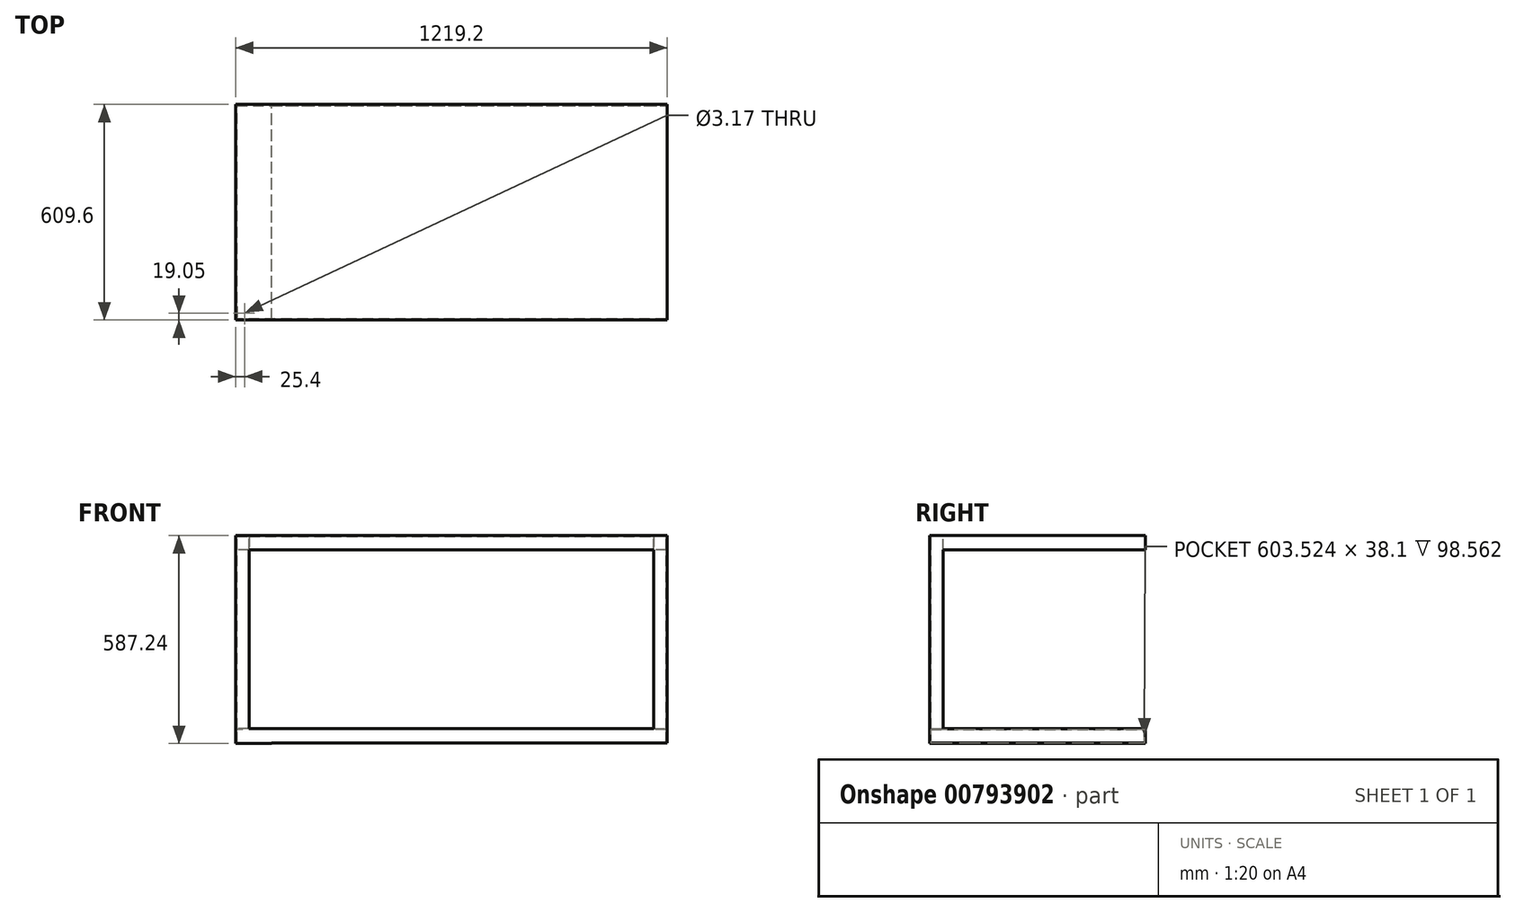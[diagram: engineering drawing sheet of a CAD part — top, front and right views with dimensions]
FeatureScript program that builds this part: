
annotation { "Feature Type Name" : "Feature", "Feature Type Description" : "" }
export const myFeature = defineFeature(function(context is Context, id is Id, definition is map)
    precondition{}
    {
        {
            var Q0;
            Q0=qCreatedBy(makeId("Top.planeOp"),FACE);
            var sketch = newSketch(context, id + "F0", { "sketchPlane" : qUnion([Q0])});
            skLineSegment(sketch, "E0.bottom", {"start": v(609.6, 304.8) * mm, "end": v(-609.6, 304.8) * mm});
            skLineSegment(sketch, "E0.top", {"start": v(609.6, -304.8) * mm, "end": v(-609.6, -304.8) * mm});
            skLineSegment(sketch, "E0.left", {"start": v(609.6, 304.8) * mm, "end": v(609.6, -304.8) * mm});
            skLineSegment(sketch, "E0.right", {"start": v(-609.6, 304.8) * mm, "end": v(-609.6, -304.8) * mm});
            skPoint(sketch, "E0.middle", {"position": v(0, 0) * mm});
            skSolve(sketch);
        }
        {
            var Q0;
            Q0=qSketchRegion(id+"F0",true);
            extrude(context, id + "F1", {"entities" : qUnion([Q0]), "oppositeDirection" : true, "depth" : 1.52 * mm, "offsetDistance" : 25.4 * mm});
        }
        {
            var Q0;
            Q0=makeQuery(id+"F1.opExtrude","CAP_FACE",FACE,{"disambiguationData":[OSD([sQuery(id+"F0.wireOp",EDGE,"E0.bottom"),sQuery(id+"F0.wireOp",EDGE,"E0.top"),sQuery(id+"F0.wireOp",EDGE,"E0.left"),sQuery(id+"F0.wireOp",EDGE,"E0.right")])],"isStart":false});
            var sketch = newSketch(context, id + "F2", { "sketchPlane" : qUnion([Q0])});
            skLineSegment(sketch, "E1", {"start": v(-609.6, 304.8) * mm, "end": v(609.6, 304.8) * mm});
            skLineSegment(sketch, "E2", {"start": v(609.6, 304.8) * mm, "end": v(609.6, -304.8) * mm});
            skLineSegment(sketch, "E3", {"start": v(609.6, -304.8) * mm, "end": v(-609.6, -304.8) * mm});
            skLineSegment(sketch, "E4", {"start": v(-609.6, -304.8) * mm, "end": v(-609.6, 304.8) * mm});
            skLineSegment(sketch, "E5.0", {"start": v(-608.08, -303.28) * mm, "end": v(-608.08, 303.28) * mm});
            skLineSegment(sketch, "E6.0", {"start": v(-608.08, 303.28) * mm, "end": v(608.08, 303.28) * mm});
            skLineSegment(sketch, "E7.0", {"start": v(608.08, 303.28) * mm, "end": v(608.08, -303.28) * mm});
            skLineSegment(sketch, "E8.0", {"start": v(608.08, -303.28) * mm, "end": v(-608.08, -303.28) * mm});
            skSolve(sketch);
        }
        {
            var Q0;
            Q0=qSketchRegion(id+"F2",true);
            extrude(context, id + "F3", {"entities" : qUnion([Q0]), "operationType" : NewBodyOperationType.ADD, "depth" : 38.1 * mm, "offsetDistance" : 25.4 * mm});
        }
        {
            var Q0;
            Q0=makeQuery(id+"F1.opExtrude","CAP_FACE",FACE,{"disambiguationData":[OSD([sQuery(id+"F0.wireOp",EDGE,"E0.bottom"),sQuery(id+"F0.wireOp",EDGE,"E0.top"),sQuery(id+"F0.wireOp",EDGE,"E0.left"),sQuery(id+"F0.wireOp",EDGE,"E0.right")])],"isStart":false});
            var sketch = newSketch(context, id + "F4", { "sketchPlane" : qUnion([Q0])});
            skLineSegment(sketch, "E9", {"start": v(-571.5, 304.8) * mm, "end": v(-609.6, 304.8) * mm});
            skLineSegment(sketch, "E10", {"start": v(-609.6, 304.8) * mm, "end": v(-609.6, 266.7) * mm});
            skLineSegment(sketch, "E11", {"start": v(-609.6, 266.7) * mm, "end": v(-606.56, 266.7) * mm});
            skLineSegment(sketch, "E12", {"start": v(-606.56, 266.7) * mm, "end": v(-606.56, 301.76) * mm});
            skLineSegment(sketch, "E13", {"start": v(-606.56, 301.76) * mm, "end": v(-571.5, 301.76) * mm});
            skLineSegment(sketch, "E14", {"start": v(-571.5, 301.76) * mm, "end": v(-571.5, 304.8) * mm});
            skLineSegment(sketch, "E15.MirrorCS", {"start": v(571.5, 301.76) * mm, "end": v(571.5, 304.8) * mm});
            skLineSegment(sketch, "E16.MirrorCS", {"start": v(609.6, 266.7) * mm, "end": v(606.56, 266.7) * mm});
            skLineSegment(sketch, "E17.MirrorCS", {"start": v(606.56, 301.76) * mm, "end": v(571.5, 301.76) * mm});
            skLineSegment(sketch, "E18.MirrorCS", {"start": v(606.56, 266.7) * mm, "end": v(606.56, 301.76) * mm});
            skLineSegment(sketch, "E19.MirrorCS", {"start": v(571.5, 304.8) * mm, "end": v(609.6, 304.8) * mm});
            skLineSegment(sketch, "E20.MirrorCS", {"start": v(609.6, 304.8) * mm, "end": v(609.6, 266.7) * mm});
            skSolve(sketch);
        }
        {
            var Q0;
            Q0=qSketchRegion(id+"F4",true);
            extrude(context, id + "F5", {"entities" : qUnion([Q0]), "operationType" : NewBodyOperationType.ADD, "depth" : 584.2 * mm, "offsetDistance" : 25.4 * mm});
        }
        {
            var Q0;
            Q0=makeQuery(id+"F1.opExtrude","CAP_FACE",FACE,{"disambiguationData":[OSD([sQuery(id+"F0.wireOp",EDGE,"E0.bottom"),sQuery(id+"F0.wireOp",EDGE,"E0.top"),sQuery(id+"F0.wireOp",EDGE,"E0.left"),sQuery(id+"F0.wireOp",EDGE,"E0.right")])],"isStart":true});
            cPlane(context, id + "F6", {"entities" : qUnion([Q0]), "cplaneType" : CPlaneType.OFFSET, "offset" : 546.1 * mm, "oppositeDirection" : true, "width" : 152.4 * mm, "height" : 152.4 * mm});
        }
        {
            var Q0;
            Q0=qCreatedBy(id+"F6.planeOp",FACE);
            var sketch = newSketch(context, id + "F7", { "sketchPlane" : qUnion([Q0])});
            skLineSegment(sketch, "E21.bottom", {"start": v(-609.6, 304.8) * mm, "end": v(609.6, 304.8) * mm});
            skLineSegment(sketch, "E21.top", {"start": v(-609.6, -304.8) * mm, "end": v(609.6, -304.8) * mm});
            skLineSegment(sketch, "E21.left", {"start": v(-609.6, 304.8) * mm, "end": v(-609.6, -304.8) * mm});
            skLineSegment(sketch, "E21.right", {"start": v(609.6, 304.8) * mm, "end": v(609.6, -304.8) * mm});
            skPoint(sketch, "E21.middle", {"position": v(0, 0) * mm});
            skSolve(sketch);
        }
        {
            var Q0;
            Q0=qSketchRegion(id+"F7",true);
            extrude(context, id + "F8", {"entities" : qUnion([Q0]), "operationType" : NewBodyOperationType.ADD, "oppositeDirection" : true, "depth" : 1.52 * mm, "offsetDistance" : 25.4 * mm});
        }
        {
            var Q0;
            Q0=makeQuery(id+"F8.opExtrude","CAP_FACE",FACE,{"disambiguationData":[OSD([sQuery(id+"F7.wireOp",EDGE,"E21.bottom"),sQuery(id+"F7.wireOp",EDGE,"E21.top"),sQuery(id+"F7.wireOp",EDGE,"E21.left"),sQuery(id+"F7.wireOp",EDGE,"E21.right")])],"isStart":false});
            var sketch = newSketch(context, id + "F9", { "sketchPlane" : qUnion([Q0])});
            skLineSegment(sketch, "E22.bottom", {"start": v(-609.6, 304.8) * mm, "end": v(609.6, 304.8) * mm});
            skLineSegment(sketch, "E22.top", {"start": v(-609.6, -304.8) * mm, "end": v(609.6, -304.8) * mm});
            skLineSegment(sketch, "E22.left", {"start": v(-609.6, 304.8) * mm, "end": v(-609.6, -304.8) * mm});
            skLineSegment(sketch, "E22.right", {"start": v(609.6, 304.8) * mm, "end": v(609.6, -304.8) * mm});
            skPoint(sketch, "E22.middle", {"position": v(0, 0) * mm});
            skLineSegment(sketch, "E23.bottom", {"start": v(-606.56, 301.76) * mm, "end": v(606.56, 301.76) * mm});
            skLineSegment(sketch, "E23.top", {"start": v(-606.56, -301.76) * mm, "end": v(606.56, -301.76) * mm});
            skLineSegment(sketch, "E23.left", {"start": v(-606.56, 301.76) * mm, "end": v(-606.56, -301.76) * mm});
            skLineSegment(sketch, "E23.right", {"start": v(606.56, 301.76) * mm, "end": v(606.56, -301.76) * mm});
            skSolve(sketch);
        }
        {
            var Q0;
            Q0=qSketchRegion(id+"F9",true);
            extrude(context, id + "F10", {"entities" : qUnion([Q0]), "operationType" : NewBodyOperationType.ADD, "depth" : 38.1 * mm, "offsetDistance" : 25.4 * mm});
        }
        {
            var Q0;
            {var subQ0=sQuery(id+"F4.wireOp",EDGE,"E19.MirrorCS");var subQ1=sQuery(id+"F4.wireOp",EDGE,"E20.MirrorCS");var subQ2=sQuery(id+"F4.wireOp",EDGE,"E17.MirrorCS");var subQ3=sQuery(id+"F4.wireOp",EDGE,"E15.MirrorCS");var subQ4=sQuery(id+"F4.wireOp",EDGE,"E16.MirrorCS");var subQ5=sQuery(id+"F4.wireOp",EDGE,"E18.MirrorCS");var subQ6=sQuery(id+"F4.wireOp",EDGE,"E9");var subQ7=sQuery(id+"F4.wireOp",EDGE,"E10");var subQ8=sQuery(id+"F4.wireOp",EDGE,"E13");var subQ9=sQuery(id+"F4.wireOp",EDGE,"E14");var subQ10=sQuery(id+"F4.wireOp",EDGE,"E12");var subQ11=sQuery(id+"F4.wireOp",EDGE,"E11");Q0=makeQuery(id+"F10.boolean.opBoolean","MERGE",FACE,{"derivedFrom":[makeQuery(id+"F5.opExtrude","CAP_FACE",FACE,{"disambiguationData":[OSD([subQ11,subQ10,subQ9,subQ8,subQ7,subQ6])],"isStart":false}),makeQuery(id+"F5.opExtrude","CAP_FACE",FACE,{"disambiguationData":[OSD([subQ5,subQ4,subQ3,subQ2,subQ1,subQ0])],"isStart":false}),makeQuery(id+"F0JGexphdKmqHas_1.1.F5.opExtrude","CAP_FACE",FACE,{"disambiguationData":[OSD([subQ11,subQ10,subQ9,subQ8,subQ7,subQ6])],"isStart":false}),makeQuery(id+"F0JGexphdKmqHas_1.1.F5.opExtrude","CAP_FACE",FACE,{"disambiguationData":[OSD([subQ5,subQ4,subQ3,subQ2,subQ1,subQ0])],"isStart":false}),makeQuery(id+"F10.opExtrude","CAP_FACE",FACE,{"disambiguationData":[OSD([sQuery(id+"F9.wireOp",EDGE,"E22.bottom"),sQuery(id+"F9.wireOp",EDGE,"E22.top"),sQuery(id+"F9.wireOp",EDGE,"E22.left"),sQuery(id+"F9.wireOp",EDGE,"E22.right"),sQuery(id+"F9.wireOp",EDGE,"E23.bottom"),sQuery(id+"F9.wireOp",EDGE,"E23.top"),sQuery(id+"F9.wireOp",EDGE,"E23.left"),sQuery(id+"F9.wireOp",EDGE,"E23.right")])],"isStart":false})]});}
            var sketch = newSketch(context, id + "F11", { "sketchPlane" : qUnion([Q0])});
            skLineSegment(sketch, "E24.bottom", {"start": v(-609.6, 304.8) * mm, "end": v(-508, 304.8) * mm});
            skLineSegment(sketch, "E24.top", {"start": v(-609.6, -304.8) * mm, "end": v(-508, -304.8) * mm});
            skLineSegment(sketch, "E24.left", {"start": v(-609.6, 304.8) * mm, "end": v(-609.6, -304.8) * mm});
            skLineSegment(sketch, "E24.right", {"start": v(-508, 304.8) * mm, "end": v(-508, -304.8) * mm});
            skSolve(sketch);
        }
        {
            var Q0;
            Q0=qSketchRegion(id+"F11",true);
            extrude(context, id + "F12", {"entities" : qUnion([Q0]), "operationType" : NewBodyOperationType.ADD, "depth" : 1.52 * mm, "offsetDistance" : 25.4 * mm});
        }
        {
            var Q0;
            Q0=makeQuery(id+"F12.opExtrude","CAP_FACE",FACE,{"disambiguationData":[OSD([sQuery(id+"F11.wireOp",EDGE,"E24.bottom"),sQuery(id+"F11.wireOp",EDGE,"E24.top"),sQuery(id+"F11.wireOp",EDGE,"E24.left"),sQuery(id+"F11.wireOp",EDGE,"E24.right")])],"isStart":false});
            var sketch = newSketch(context, id + "F13", { "sketchPlane" : qUnion([Q0])});
            skCircle(sketch, "E25", {"center": v(-584.2, 285.75) * mm, "radius": 1.59 * mm});
            skSolve(sketch);
        }
        {
            var Q0;
            Q0=qSketchRegion(id+"F13",true);
            extrude(context, id + "F14", {"entities" : qUnion([Q0]), "operationType" : NewBodyOperationType.REMOVE, "oppositeDirection" : true, "depth" : 1.65 * mm, "offsetDistance" : 25.4 * mm});
        }
    });
